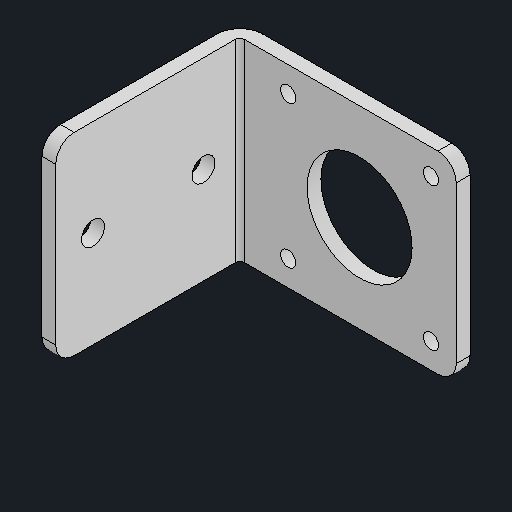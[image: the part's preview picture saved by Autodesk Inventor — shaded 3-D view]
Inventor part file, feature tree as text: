
AUTODESK INVENTOR PART (.ipt)
format: ipt  version: 2024.2 (Build 282272000, 272)  size: 104,960 bytes
history: native  units: mm
features: other x1, fillet x1
ambient origin geometry x8: Origin, YZ Plane, XZ Plane, XY Plane, X Axis, Y Axis, Z Axis, Center Point
bodies: Body1 (feature_tree)
feature tree (2):
  other  "솔리드1"
  fillet  "Fillet3"  [1 undecoded]
note: 1 required parameter value undecoded (feature->parameter linkage not recoverable at this tier; creation-order binding heuristic only, values carry confidence <= 0.55)
